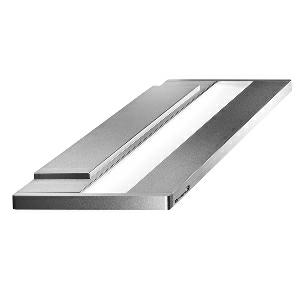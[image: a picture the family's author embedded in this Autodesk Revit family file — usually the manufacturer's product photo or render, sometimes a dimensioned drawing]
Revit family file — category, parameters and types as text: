
# Revit family: zera_bed_-_zew_9000_vtl_d_-_ul_dali_00812998_d5eb
name_source: partatom
category: Lighting Fixtures
units: mm (PartAtom-declared; Revit-internal decimal feet)

## family parameters
Cut with Voids When Loaded = No
Host = Face
Light Source = No
Part Type = Normal
Room Calculation Point = No
Round Connector Dimension = Use Diameter
Shared = No

## types (1)
- AL+UL (1 x LED VTL, 7800 lm, 3000-6500K)
    Apparent Load = 82 VA
    Approval mark = CE
    CIE Flux Codes = 45 81 99 31 100
    Color Rendering = 80-89
    Color Temperature = 3000-6500K
    Default Elevation = 2000 mm  [stored 6.56168 ft]
    Description = ZEW 9000/VTL/D|Wall-mounted luminaire|light source:   Cold white   |work equipment: Power supply unit|luminous flux: 8890 lm|light distribution: Direct/indirect|class of protection: I|technology: Switchable|mains lead: Connector 5 pin|glare control: Diffusor|special features: General light, indirect, 3000K-6500K, Ra80, Biodynamic light VTL, DIN EN 60598-2-25, External control device required for DALI Device Type 6, Reading light, direct, 2700K, Ra90, dir 4K 36W Ra95|
    Frequency = 50 Hz, 60 Hz
    Height = 20 mm  [stored 0.0656168 ft]
    Lamp = 1 x LED VTL
    Lamp Light Flux = 7800 lm
    Lamp count = 1
    Length = 1050 mm
    Luminous efficacy = 95 lm/W
    Manufacturer = Waldmann
    ModVariant = No
    Model = 00812998
    Mounting Place = Wall
    Mounting Type = Surface mounted
    Number of Poles = 1
    OnlyDefault = Yes
    Power Factor = 1
    Product Name = ZERA.bed - ZEW 9000/VTL/D - UL/DALI
    Product group = Wall mounted Luminaire
    ProductGroupID = 20
    Protection Class = Protection class I
    Protection Degree = IP 20
    RLX_Detail_Level = 1
    RLX_Emergency_Light_Flux = 0 lm
    RLX_Emergency_Type = 0
    RLX_Emergency_Type_DB = No
    RlxData = <blob elided: 60633 chars, md5=ad82d595>
    Socket = socket
    Standby Power = 0 W
    System Light Flux = 7800 lm
    System Power = 82 W
    Type Comments = General and Examation Light
    Type Image = zera_bed.jpg
    URL = http://relux.com
    VarID = al_ul_37f9
    Voltage = 230 V
    Voltage Range = 220-240 V
    Weight = 0.00 kg
    Width = 230 mm

note: [stored X ft] marks values corroborated as IEEE doubles in the binary element streams (Revit-internal decimal feet)

## geometry (parser evidence)
native form markers: Blend x4, Sweep x14
no freeform markers — native parametric forms only
